# Revit family: ATPSF-201-208-S REV2
name_source: partatom
category: Mechanical Equipment
revit_build: Autodesk Revit 2017 (Build: 20190508_0315(x64)
units: mm (PartAtom-declared; Revit-internal decimal feet)

## family parameters
Always vertical = Yes
Cut with Voids When Loaded = No
OmniClass Number = 23.75.00.00
OmniClass Title = Climate Control (HVAC)
Part Type = Normal
Room Calculation Point = No
Round Connector Dimension = Use Diameter
Shared = No
Work Plane-Based = No

## types (6) — shared parameters
1/3HP = No
115/208/230 Volts = No
1HP = No
208/230/460 Volts = Yes
Base Lenglth = 5' - 5 1/2"
Base Width = 2' - 6 1/2"
Description = Automatic Fuel Oil Transfer Pump Set
Manufacturer = Preferred Utilities MFG
Phase = 3
URL = www.preferred-mfg.com
Weight = 700.00 lbf

## per-type parameters (varying)
| type | 1-1/2HP | 1/2HP | 2HP | 3/4HP | Base Height | G.P.H. Oil #2 / #4 | HP | Inlet Diameter | Inlet Radius | Model | Outlet Diameter | Outlet Radius | PSI | RPM | Relief Valve Diameter | Relief Valve Radius |
| 201-S_375/423 GPH_50 PSI_1/2 HP_1140 RPM | No | Yes | No | No | 6' - 4 5/8" | 375 / 423 | 1/2 | 0' - 1" | 0' - 0 1/2" | ATPSF-201-S | 0' - 1" | 0' - 0 1/2" | 50.00 psi | 1140 | 0' - 0 1/2" | 0' - 0 1/4" |
| 202-S_340/408 GPH_100 PSI_3/4 HP_1140 RPM | No | No | No | Yes | 6' - 4 5/8" | 340 / 408 | 3/4 | 0' - 1" | 0' - 0 1/2" | ATPSF-202-S | 0' - 1" | 0' - 0 1/2" | 100.00 psi | 1140 | 0' - 0 1/2" | 0' - 0 1/4" |
| 203-S_757/875 GPH_50 PSI_3/4 HP_1140 RPM | No | No | No | Yes | 6' - 9 5/8" | 757 / 875 | 3/4 | 0' - 1 1/2" | 0' - 0 3/4" | ATPSF-203-S | 0' - 1 1/2" | 0' - 0 3/4" | 50.00 psi | 1140 | 0' - 0 3/4" | 0' - 0 3/8" |
| 204-S_714/881 GPH_100 PSI_1-1/2 HP_1165 RPM | Yes | No | No | No | 6' - 9 5/8" | 714 / 881 | 1-1/2 | 0' - 1 1/2" | 0' - 0 3/4" | ATPSF-204-S | 0' - 1 1/2" | 0' - 0 3/4" | 100.00 psi | 1165 | 0' - 0 3/4" | 0' - 0 3/8" |
| 205-S_1095/1287 GPH_50 PSI_1-1/2 HP_1165 RPM | Yes | No | No | No | 6' - 9 5/8" | 1095 / 1287 | 1-1/2 | 0' - 1 1/2" | 0' - 0 3/4" | ATPSF-205-S | 0' - 1 1/2" | 0' - 0 3/4" | 50.00 psi | 1165 | 0' - 1 1/4" | 0' - 0 5/8" |
| 206-S_1005/1277 GPH_100 PSI_2 HP_1170 RPM | No | No | Yes | No | 6' - 9 5/8" | 1005 / 1277 | 2 | 0' - 1 1/2" | 0' - 0 3/4" | ATPSF-206-S | 0' - 1 1/2" | 0' - 0 3/4" | 100.00 psi | 1170 | 0' - 1" | 0' - 0 1/2" |

## geometry (parser evidence)
native form markers: Sweep x1
no freeform markers — native parametric forms only
